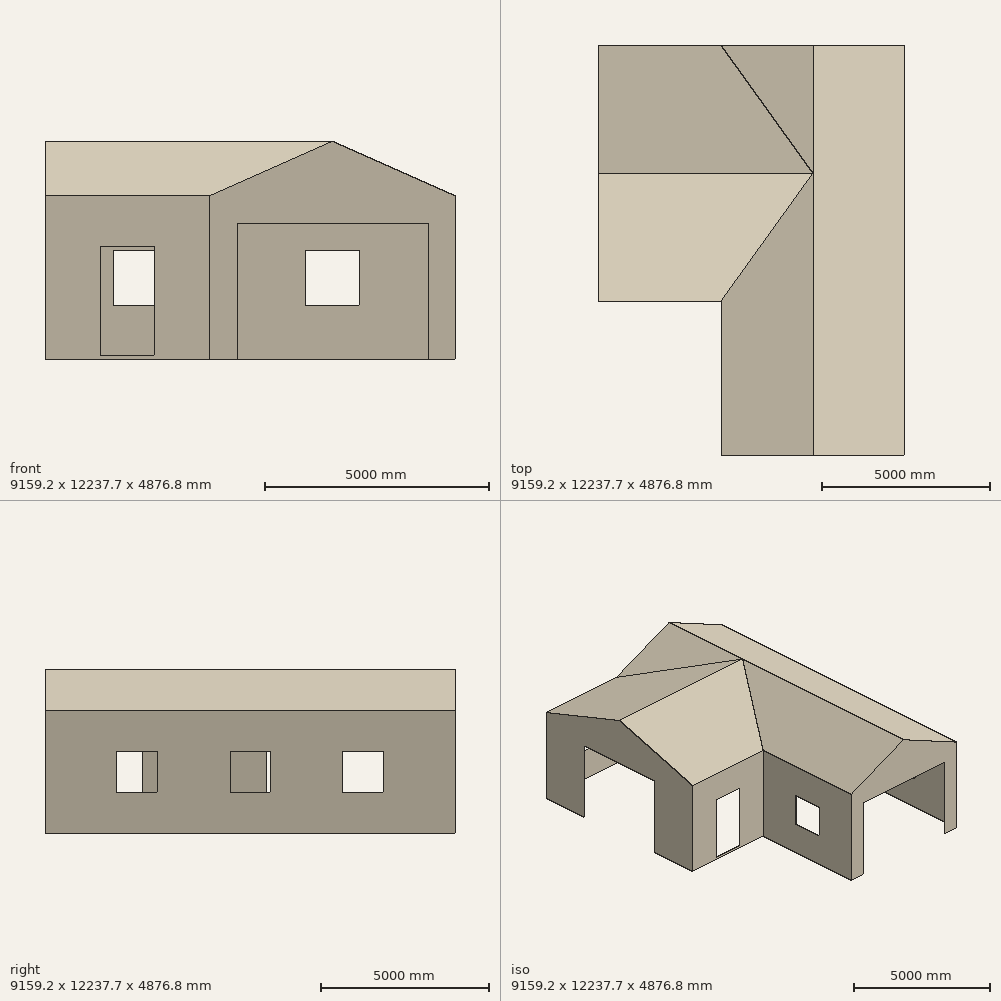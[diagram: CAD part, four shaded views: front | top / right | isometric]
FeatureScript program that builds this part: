
annotation { "Feature Type Name" : "Feature", "Feature Type Description" : "" }
export const myFeature = defineFeature(function(context is Context, id is Id, definition is map)
    precondition{}
    {
        {
            var Q0;
            Q0=qCreatedBy(makeId("Front.planeOp"),FACE);
            var sketch = newSketch(context, id + "F0", { "sketchPlane" : qUnion([Q0])});
            skLineSegment(sketch, "E0", {"start": v(0, 0) * mm, "end": v(5486.4, 0) * mm});
            skLineSegment(sketch, "E1", {"start": v(5486.4, 0) * mm, "end": v(5486.4, 3657.6) * mm});
            skLineSegment(sketch, "E2", {"start": v(5486.4, 3657.6) * mm, "end": v(2743.2, 4876.8) * mm});
            skLineSegment(sketch, "E3", {"start": v(2743.2, 4876.8) * mm, "end": v(0, 3657.6) * mm});
            skLineSegment(sketch, "E4", {"start": v(0, 3657.6) * mm, "end": v(0, 0) * mm});
            skPoint(sketch, "E5", {"position": v(2743.2, 0) * mm});
            skSolve(sketch);
        }
        {
            var Q0;
            Q0=makeQuery(id+"F0.imprint","IMPRINT",FACE,{"disambiguationData":[TD([[makeQuery(id+"F0.imprint","IMPRINT",EDGE,{"derivedFrom":sQuery(id+"F0.wireOp",EDGE,"E0")}),1.0]])]});
            extrude(context, id + "F1", {"entities" : qUnion([Q0]), "depth" : 12207.24 * mm, "offsetDistance" : 30.48 * mm});
        }
        {
            var Q0;
            Q0=makeQuery(id+"F1.opExtrude","SWEPT_FACE",FACE,{"disambiguationData":[OSD([sQuery(id+"F0.wireOp",EDGE,"E4")])]});
            var sketch = newSketch(context, id + "F2", { "sketchPlane" : qUnion([Q0])});
            skLineSegment(sketch, "E6", {"start": v(0, 0) * mm, "end": v(0, 3657.6) * mm});
            skLineSegment(sketch, "E7.0", {"start": v(12207.24, 4876.8) * mm, "end": v(0, 4876.8) * mm});
            skLineSegment(sketch, "E8.0", {"start": v(12207.24, 4876.8) * mm, "end": v(0, 4876.8) * mm, "construction": true});
            skLineSegment(sketch, "E9", {"start": v(0, 3657.6) * mm, "end": v(3817.62, 4876.8) * mm});
            skLineSegment(sketch, "E10", {"start": v(3817.62, 4876.8) * mm, "end": v(7635.24, 3657.6) * mm});
            skLineSegment(sketch, "E11", {"start": v(7635.24, 3657.6) * mm, "end": v(7635.24, 0) * mm});
            skLineSegment(sketch, "E12", {"start": v(7635.24, 0) * mm, "end": v(0, 0) * mm});
            skPoint(sketch, "E13", {"position": v(3817.62, 0) * mm});
            skSolve(sketch);
        }
        {
            var Q0;
            Q0=qSketchRegion(id+"F2",true);
            extrude(context, id + "F3", {"entities" : qUnion([Q0]), "operationType" : NewBodyOperationType.ADD, "depth" : 3672.84 * mm, "offsetDistance" : 30.48 * mm, "hasSecondDirection" : true, "secondDirectionOppositeDirection" : true, "secondDirectionDepth" : 2743.2 * mm});
        }
        {
            var Q0;
            {var subQ0=sQuery(id+"F0.wireOp",EDGE,"E0");Q0=makeQuery(id+"F5.boolean.opBoolean","MERGE",FACE,{"derivedFrom":[makeQuery(id+"F3.boolean.opBoolean","MERGE",FACE,{"derivedFrom":[makeQuery(id+"F1.opExtrude","SWEPT_FACE",FACE,{"disambiguationData":[OSD([subQ0])]}),makeQuery(id+"F3.opExtrude","SWEPT_FACE",FACE,{"disambiguationData":[OSD([sQuery(id+"F2.wireOp",EDGE,"E12")])]})]}),makeQuery(id+"F5.opExtrude","SWEPT_FACE",FACE,{"disambiguationData":[OSD([subQ0])]})]});}
            shell(context, id + "F4", {"entities" : qUnion([Q0]), "thickness" : 7.62 * mm});
        }
        {
            var Q0;
            Q0=makeQuery(id+"F1.opExtrude","CAP_FACE",FACE,{"disambiguationData":[OSD([sQuery(id+"F0.wireOp",EDGE,"E0"),sQuery(id+"F0.wireOp",EDGE,"E1"),sQuery(id+"F0.wireOp",EDGE,"E2"),sQuery(id+"F0.wireOp",EDGE,"E3"),sQuery(id+"F0.wireOp",EDGE,"E4")])],"isStart":false});
            extrude(context, id + "F5", {"entities" : qUnion([Q0]), "operationType" : NewBodyOperationType.ADD, "depth" : 30.48 * mm, "offsetDistance" : 30.48 * mm});
        }
        {
            var Q0;
            Q0=makeQuery(id+"F5.opExtrude","CAP_FACE",FACE,{"disambiguationData":[OSD([sQuery(id+"F0.wireOp",EDGE,"E0"),sQuery(id+"F0.wireOp",EDGE,"E1"),sQuery(id+"F0.wireOp",EDGE,"E2"),sQuery(id+"F0.wireOp",EDGE,"E3"),sQuery(id+"F0.wireOp",EDGE,"E4")])],"isStart":false});
            var sketch = newSketch(context, id + "F6", { "sketchPlane" : qUnion([Q0])});
            skLineSegment(sketch, "E14.bottom", {"start": v(609.6, 0) * mm, "end": v(4876.8, 0) * mm});
            skLineSegment(sketch, "E14.top", {"start": v(609.6, 3048) * mm, "end": v(4876.8, 3048) * mm});
            skLineSegment(sketch, "E14.left", {"start": v(609.6, 0) * mm, "end": v(609.6, 3048) * mm});
            skLineSegment(sketch, "E14.right", {"start": v(4876.8, 0) * mm, "end": v(4876.8, 3048) * mm});
            skSolve(sketch);
        }
        {
            var Q0;
            Q0=qSketchRegion(id+"F6",true);
            extrude(context, id + "F7", {"entities" : qUnion([Q0]), "operationType" : NewBodyOperationType.REMOVE, "oppositeDirection" : true, "depth" : 152.4 * mm, "offsetDistance" : 30.48 * mm});
        }
        {
            var Q0;
            Q0=makeQuery(id+"F3.opExtrude","CAP_FACE",FACE,{"disambiguationData":[OSD([sQuery(id+"F2.wireOp",EDGE,"E6"),sQuery(id+"F2.wireOp",EDGE,"E9"),sQuery(id+"F2.wireOp",EDGE,"E10"),sQuery(id+"F2.wireOp",EDGE,"E11"),sQuery(id+"F2.wireOp",EDGE,"E12")])],"isStart":false});
            var sketch = newSketch(context, id + "F8", { "sketchPlane" : qUnion([Q0])});
            skLineSegment(sketch, "E15.bottom", {"start": v(1981.2, 0) * mm, "end": v(5638.8, 0) * mm});
            skLineSegment(sketch, "E15.top", {"start": v(1981.2, 3048) * mm, "end": v(5638.8, 3048) * mm});
            skLineSegment(sketch, "E15.left", {"start": v(1981.2, 0) * mm, "end": v(1981.2, 3048) * mm});
            skLineSegment(sketch, "E15.right", {"start": v(5638.8, 0) * mm, "end": v(5638.8, 3048) * mm});
            skSolve(sketch);
        }
        {
            var Q0;
            Q0=qSketchRegion(id+"F8",true);
            extrude(context, id + "F9", {"entities" : qUnion([Q0]), "operationType" : NewBodyOperationType.REMOVE, "oppositeDirection" : true, "depth" : 152.4 * mm, "offsetDistance" : 30.48 * mm});
        }
        {
            var Q0;
            Q0=makeQuery(id+"F3.opExtrude","SWEPT_FACE",FACE,{"disambiguationData":[OSD([sQuery(id+"F2.wireOp",EDGE,"E11")])]});
            var sketch = newSketch(context, id + "F10", { "sketchPlane" : qUnion([Q0])});
            skLineSegment(sketch, "E16.bottom", {"start": v(-2453.64, 100.58) * mm, "end": v(-1234.44, 100.58) * mm});
            skLineSegment(sketch, "E16.top", {"start": v(-2453.64, 2538.98) * mm, "end": v(-1234.44, 2538.98) * mm});
            skLineSegment(sketch, "E16.left", {"start": v(-2453.64, 100.58) * mm, "end": v(-2453.64, 2538.98) * mm});
            skLineSegment(sketch, "E16.right", {"start": v(-1234.44, 100.58) * mm, "end": v(-1234.44, 2538.98) * mm});
            skSolve(sketch);
        }
        {
            var Q0;
            Q0=qSketchRegion(id+"F10",true);
            extrude(context, id + "F11", {"entities" : qUnion([Q0]), "operationType" : NewBodyOperationType.REMOVE, "oppositeDirection" : true, "depth" : 152.4 * mm, "offsetDistance" : 30.48 * mm});
        }
        {
            var Q0;
            {var subQ0=sQuery(id+"F0.wireOp",EDGE,"E1");Q0=makeQuery(id+"F5.boolean.opBoolean","MERGE",FACE,{"derivedFrom":[makeQuery(id+"F1.opExtrude","SWEPT_FACE",FACE,{"disambiguationData":[OSD([subQ0])]}),makeQuery(id+"F5.opExtrude","SWEPT_FACE",FACE,{"disambiguationData":[OSD([subQ0])]})]});}
            var sketch = newSketch(context, id + "F12", { "sketchPlane" : qUnion([Q0])});
            skLineSegment(sketch, "E17.bottom", {"start": v(-10104.12, 2438.4) * mm, "end": v(-8884.92, 2438.4) * mm});
            skLineSegment(sketch, "E17.top", {"start": v(-10104.12, 1219.2) * mm, "end": v(-8884.92, 1219.2) * mm});
            skLineSegment(sketch, "E17.left", {"start": v(-10104.12, 2438.4) * mm, "end": v(-10104.12, 1219.2) * mm});
            skLineSegment(sketch, "E17.right", {"start": v(-8884.92, 2438.4) * mm, "end": v(-8884.92, 1219.2) * mm});
            skLineSegment(sketch, "E18.bottom", {"start": v(-6728.46, 2438.4) * mm, "end": v(-5509.26, 2438.4) * mm});
            skLineSegment(sketch, "E18.top", {"start": v(-6728.46, 1219.2) * mm, "end": v(-5509.26, 1219.2) * mm});
            skLineSegment(sketch, "E18.left", {"start": v(-6728.46, 2438.4) * mm, "end": v(-6728.46, 1219.2) * mm});
            skLineSegment(sketch, "E18.right", {"start": v(-5509.26, 2438.4) * mm, "end": v(-5509.26, 1219.2) * mm});
            skLineSegment(sketch, "E19.bottom", {"start": v(-3375.66, 2438.4) * mm, "end": v(-2156.46, 2438.4) * mm});
            skLineSegment(sketch, "E19.top", {"start": v(-3375.66, 1219.2) * mm, "end": v(-2156.46, 1219.2) * mm});
            skLineSegment(sketch, "E19.left", {"start": v(-3375.66, 2438.4) * mm, "end": v(-3375.66, 1219.2) * mm});
            skLineSegment(sketch, "E19.right", {"start": v(-2156.46, 2438.4) * mm, "end": v(-2156.46, 1219.2) * mm});
            skPoint(sketch, "E20", {"position": v(-6118.86, 2438.4) * mm});
            skPoint(sketch, "E21", {"position": v(-6118.86, 3657.6) * mm});
            skSolve(sketch);
        }
        {
            var Q0;
            Q0=qSketchRegion(id+"F12",true);
            extrude(context, id + "F13", {"entities" : qUnion([Q0]), "operationType" : NewBodyOperationType.REMOVE, "oppositeDirection" : true, "depth" : 100.58 * mm, "offsetDistance" : 30.48 * mm});
        }
        {
            var Q0;
            Q0=makeQuery(id+"F3.boolean.opBoolean","MERGE",FACE,{"derivedFrom":[makeQuery(id+"F1.opExtrude","CAP_FACE",FACE,{"disambiguationData":[OSD([sQuery(id+"F0.wireOp",EDGE,"E0"),sQuery(id+"F0.wireOp",EDGE,"E1"),sQuery(id+"F0.wireOp",EDGE,"E2"),sQuery(id+"F0.wireOp",EDGE,"E3"),sQuery(id+"F0.wireOp",EDGE,"E4")])],"isStart":true}),makeQuery(id+"F3.opExtrude","SWEPT_FACE",FACE,{"disambiguationData":[OSD([sQuery(id+"F2.wireOp",EDGE,"E6")])]})]});
            var sketch = newSketch(context, id + "F14", { "sketchPlane" : qUnion([Q0])});
            skLineSegment(sketch, "E22.bottom", {"start": v(-3352.8, 2438.4) * mm, "end": v(-2133.6, 2438.4) * mm});
            skLineSegment(sketch, "E22.top", {"start": v(-3352.8, 1219.2) * mm, "end": v(-2133.6, 1219.2) * mm});
            skLineSegment(sketch, "E22.left", {"start": v(-3352.8, 2438.4) * mm, "end": v(-3352.8, 1219.2) * mm});
            skLineSegment(sketch, "E22.right", {"start": v(-2133.6, 2438.4) * mm, "end": v(-2133.6, 1219.2) * mm});
            skLineSegment(sketch, "E23.bottom", {"start": v(929.64, 2438.4) * mm, "end": v(2148.84, 2438.4) * mm});
            skLineSegment(sketch, "E23.top", {"start": v(929.64, 1219.2) * mm, "end": v(2148.84, 1219.2) * mm});
            skLineSegment(sketch, "E23.left", {"start": v(929.64, 2438.4) * mm, "end": v(929.64, 1219.2) * mm});
            skLineSegment(sketch, "E23.right", {"start": v(2148.84, 2438.4) * mm, "end": v(2148.84, 1219.2) * mm});
            skPoint(sketch, "E24", {"position": v(-2743.2, 2438.4) * mm});
            skPoint(sketch, "E25", {"position": v(-2743.2, 4876.8) * mm});
            skSolve(sketch);
        }
        {
            var Q0;
            Q0=qSketchRegion(id+"F14",true);
            extrude(context, id + "F15", {"entities" : qUnion([Q0]), "operationType" : NewBodyOperationType.REMOVE, "oppositeDirection" : true, "depth" : 100.58 * mm, "offsetDistance" : 30.48 * mm});
        }
        {
            var Q0;
            {var subQ0=sQuery(id+"F0.wireOp",EDGE,"E4");Q0=makeQuery(id+"F5.boolean.opBoolean","MERGE",FACE,{"derivedFrom":[makeQuery(id+"F1.opExtrude","SWEPT_FACE",FACE,{"disambiguationData":[OSD([subQ0])]}),makeQuery(id+"F5.opExtrude","SWEPT_FACE",FACE,{"disambiguationData":[OSD([subQ0])]})]});}
            var sketch = newSketch(context, id + "F16", { "sketchPlane" : qUnion([Q0])});
            skLineSegment(sketch, "E26.bottom", {"start": v(9342.12, 2438.4) * mm, "end": v(10561.32, 2438.4) * mm});
            skLineSegment(sketch, "E26.top", {"start": v(9342.12, 1219.2) * mm, "end": v(10561.32, 1219.2) * mm});
            skLineSegment(sketch, "E26.left", {"start": v(9342.12, 2438.4) * mm, "end": v(9342.12, 1219.2) * mm});
            skLineSegment(sketch, "E26.right", {"start": v(10561.32, 2438.4) * mm, "end": v(10561.32, 1219.2) * mm});
            skSolve(sketch);
        }
        {
            var Q0;
            Q0=qSketchRegion(id+"F16",true);
            extrude(context, id + "F17", {"entities" : qUnion([Q0]), "operationType" : NewBodyOperationType.REMOVE, "oppositeDirection" : true, "depth" : 100.58 * mm, "offsetDistance" : 30.48 * mm});
        }
    });
